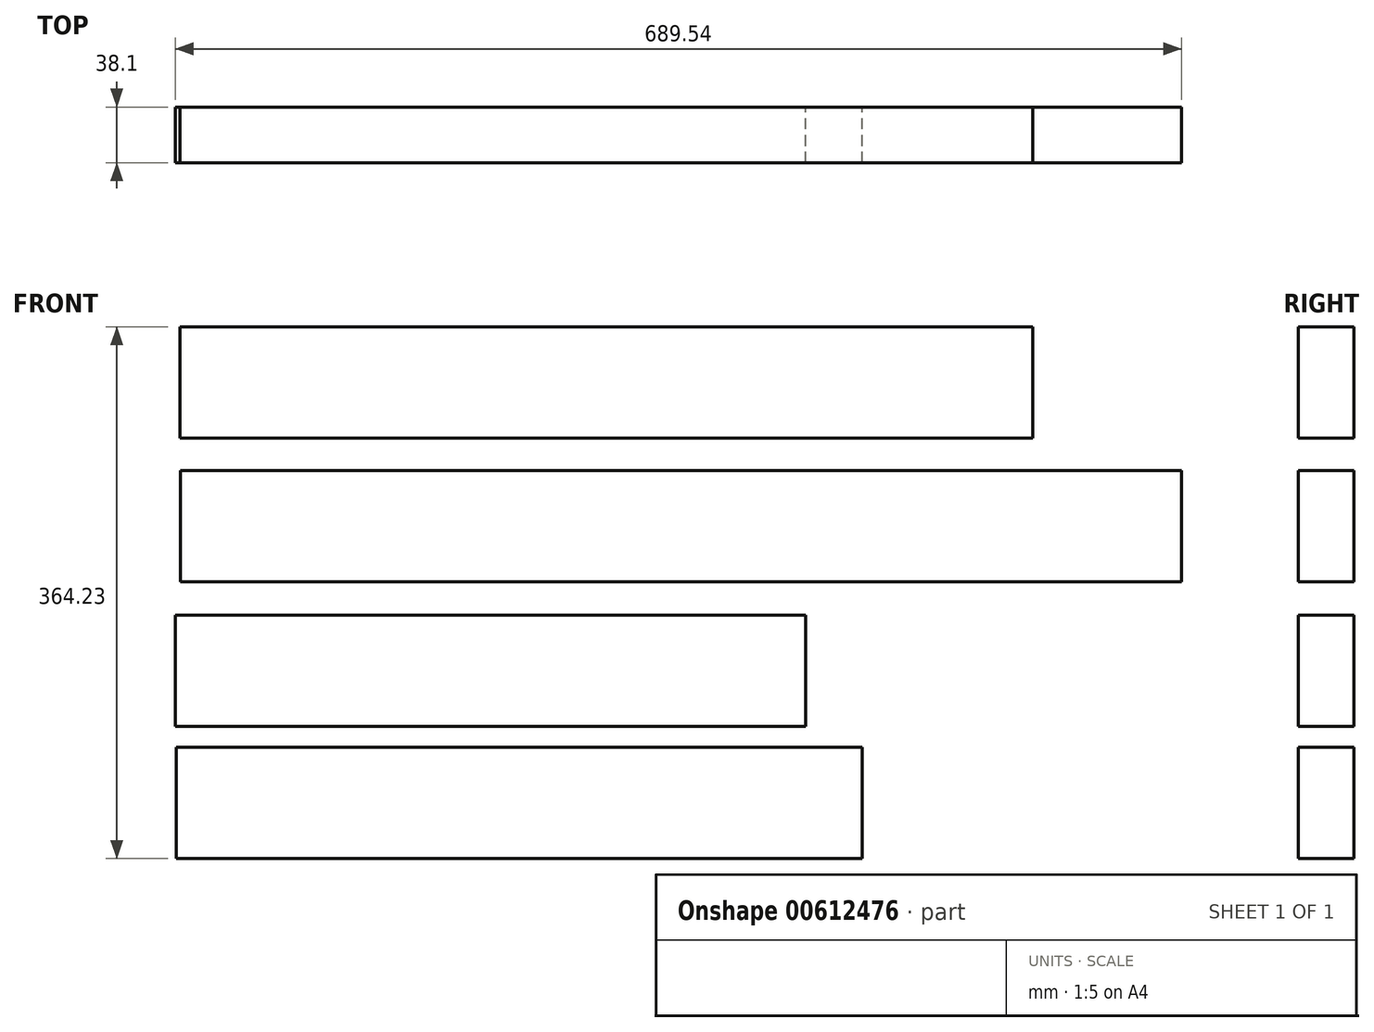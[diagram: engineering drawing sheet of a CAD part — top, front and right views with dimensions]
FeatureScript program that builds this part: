
annotation { "Feature Type Name" : "Feature", "Feature Type Description" : "" }
export const myFeature = defineFeature(function(context is Context, id is Id, definition is map)
    precondition{}
    {
        {
            var Q0;
            Q0=qCreatedBy(makeId("Front.planeOp"),FACE);
            var sketch = newSketch(context, id + "F0", { "sketchPlane" : qUnion([Q0])});
            skLineSegment(sketch, "E0.bottom", {"start": v(-63.99, 158.2) * mm, "end": v(520.21, 158.2) * mm});
            skLineSegment(sketch, "E0.top", {"start": v(-63.99, 82) * mm, "end": v(520.21, 82) * mm});
            skLineSegment(sketch, "E0.left", {"start": v(-63.99, 158.2) * mm, "end": v(-63.99, 82) * mm});
            skLineSegment(sketch, "E0.right", {"start": v(520.21, 158.2) * mm, "end": v(520.21, 82) * mm});
            skLineSegment(sketch, "E1.bottom", {"start": v(-63.65, 59.73) * mm, "end": v(622.15, 59.73) * mm});
            skLineSegment(sketch, "E1.top", {"start": v(-63.65, -16.47) * mm, "end": v(622.15, -16.47) * mm});
            skLineSegment(sketch, "E1.left", {"start": v(-63.65, 59.73) * mm, "end": v(-63.65, -16.47) * mm});
            skLineSegment(sketch, "E1.right", {"start": v(622.15, 59.73) * mm, "end": v(622.15, -16.47) * mm});
            skLineSegment(sketch, "E2.bottom", {"start": v(-67.4, -39.4) * mm, "end": v(364.4, -39.4) * mm});
            skLineSegment(sketch, "E2.top", {"start": v(-67.4, -115.6) * mm, "end": v(364.4, -115.6) * mm});
            skLineSegment(sketch, "E2.left", {"start": v(-67.4, -39.4) * mm, "end": v(-67.4, -115.6) * mm});
            skLineSegment(sketch, "E2.right", {"start": v(364.4, -39.4) * mm, "end": v(364.4, -115.6) * mm});
            skLineSegment(sketch, "E3.bottom", {"start": v(-66.54, -129.82) * mm, "end": v(403.36, -129.82) * mm});
            skLineSegment(sketch, "E3.top", {"start": v(-66.54, -206.02) * mm, "end": v(403.36, -206.02) * mm});
            skLineSegment(sketch, "E3.left", {"start": v(-66.54, -129.82) * mm, "end": v(-66.54, -206.02) * mm});
            skLineSegment(sketch, "E3.right", {"start": v(403.36, -129.82) * mm, "end": v(403.36, -206.02) * mm});
            skSolve(sketch);
        }
        {
            var Q0;
            Q0=makeQuery(id+"F0.imprint","IMPRINT",FACE,{"disambiguationData":[TD([[makeQuery(id+"F0.imprint","IMPRINT",EDGE,{"derivedFrom":sQuery(id+"F0.wireOp",EDGE,"E0.bottom")}),-1.0]])]});
            var Q1;
            Q1=makeQuery(id+"F0.imprint","IMPRINT",FACE,{"disambiguationData":[TD([[makeQuery(id+"F0.imprint","IMPRINT",EDGE,{"derivedFrom":sQuery(id+"F0.wireOp",EDGE,"E1.bottom")}),-1.0]])]});
            var Q2;
            Q2=makeQuery(id+"F0.imprint","IMPRINT",FACE,{"disambiguationData":[TD([[makeQuery(id+"F0.imprint","IMPRINT",EDGE,{"derivedFrom":sQuery(id+"F0.wireOp",EDGE,"E2.bottom")}),-1.0]])]});
            extrude(context, id + "F1", {"entities" : qUnion([Q0, Q1, Q2]), "depth" : 38.1 * mm, "offsetDistance" : 25.4 * mm});
        }
        {
            var Q0;
            Q0=makeQuery(id+"F0.imprint","IMPRINT",FACE,{"disambiguationData":[TD([[makeQuery(id+"F0.imprint","IMPRINT",EDGE,{"derivedFrom":sQuery(id+"F0.wireOp",EDGE,"E3.bottom")}),-1.0]])]});
            extrude(context, id + "F2", {"entities" : qUnion([Q0]), "depth" : 38.1 * mm, "offsetDistance" : 25.4 * mm});
        }
    });
